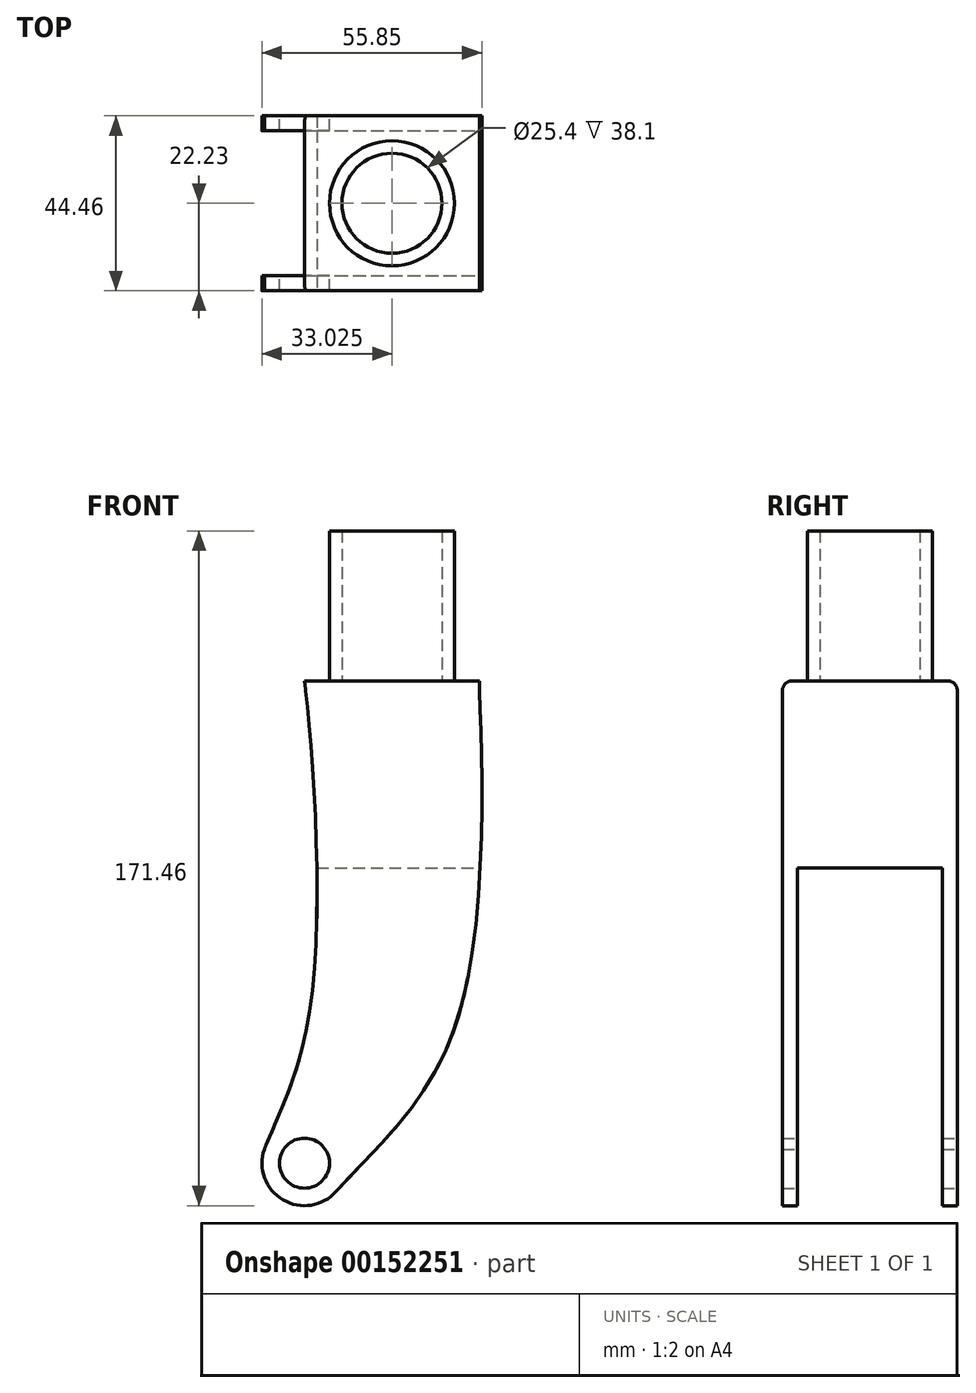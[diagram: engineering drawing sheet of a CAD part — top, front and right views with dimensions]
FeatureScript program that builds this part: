
annotation { "Feature Type Name" : "Feature", "Feature Type Description" : "" }
export const myFeature = defineFeature(function(context is Context, id is Id, definition is map)
    precondition{}
    {
        {
            var Q0;
            Q0=qCreatedBy(makeId("Front.planeOp"),FACE);
            var sketch = newSketch(context, id + "F0", { "sketchPlane" : qUnion([Q0])});
            skCircle(sketch, "E0", {"center": v(0, 0) * mm, "radius": 6.35 * mm});
            skCircle(sketch, "E1", {"center": v(0, 0) * mm, "radius": 10.8 * mm});
            skLineSegment(sketch, "E2", {"start": v(-12.15, 73.03) * mm, "end": v(17.71, 73.03) * mm, "construction": true});
            skLineSegment(sketch, "E3", {"start": v(0, 122.56) * mm, "end": v(44.45, 122.56) * mm});
            skFitSpline(sketch, "E4", {"points": [v(-10.2, 3.55) * mm, v(1.72, 41.33) * mm, v(0, 122.56) * mm], "startDerivative": vector(30.4, 74.22) * mm, "endDerivative": vector(-10.16, 76.8) * mm});
            skFitSpline(sketch, "E5", {"points": [v(8.07, -7.17) * mm, v(38.6, 35.7) * mm, v(44.45, 122.56) * mm], "startDerivative": vector(70.39, 79.18) * mm, "endDerivative": vector(-1.93, 89.44) * mm});
            skPoint(sketch, "E6", {"position": v(0, -10.8) * mm});
            skCircle(sketch, "E7", {"center": v(0, 0) * mm, "radius": 73.03 * mm, "construction": true});
            skSolve(sketch);
        }
        {
            var Q0;
            {var subQ4=sQuery(id+"F0.wireOp",EDGE,"E3");Q0=makeQuery(id+"F0.imprint","IMPRINT",FACE,{"disambiguationData":[TD([[makeQuery(id+"F0.imprint","IMPRINT",EDGE,{"derivedFrom":subQ4}),-1.0]])]});}
            var Q1;
            Q1=makeQuery(id+"F0.imprint","IMPRINT",FACE,{"disambiguationData":[TD([[makeQuery(id+"F0.imprint","IMPRINT",EDGE,{"derivedFrom":sQuery(id+"F0.wireOp",EDGE,"E0")}),-1.0]])]});
            extrude(context, id + "F1", {"entities" : qUnion([Q0, Q1]), "endBound" : BoundingType.SYMMETRIC, "depth" : 44.45 * mm});
        }
        {
            var Q0;
            Q0=makeQuery(id+"F1.opExtrude","CAP_FACE",FACE,{"disambiguationData":[OSD([sQuery(id+"F0.wireOp",EDGE,"E0"),sQuery(id+"F0.wireOp",EDGE,"E1"),sQuery(id+"F0.wireOp",EDGE,"E3"),sQuery(id+"F0.wireOp",EDGE,"E4"),sQuery(id+"F0.wireOp",EDGE,"E5")])],"isStart":false});
            var sketch = newSketch(context, id + "F2", { "sketchPlane" : qUnion([Q0])});
            skLineSegment(sketch, "E8", {"start": v(3.11, 77.02) * mm, "end": v(44.72, 77.02) * mm});
            skCircle(sketch, "E9", {"center": v(0, 0) * mm, "radius": 6.35 * mm});
            skLineSegment(sketch, "E10", {"start": v(3.15, 74.96) * mm, "end": v(44.62, 74.96) * mm});
            skLineSegment(sketch, "E11", {"start": v(44.62, 74.96) * mm, "end": v(44.72, 77.02) * mm});
            skLineSegment(sketch, "E12", {"start": v(3.11, 77.02) * mm, "end": v(3.15, 74.96) * mm});
            skSolve(sketch);
        }
        {
            var Q0;
            Q0=makeQuery(id+"F2.imprint","IMPRINT",FACE,{"disambiguationData":[TD([[makeQuery(id+"F2.imprint","IMPRINT",EDGE,{"derivedFrom":sQuery(id+"F2.wireOp",EDGE,"E9")}),-1.0]])]});
            extrude(context, id + "F3", {"entities" : qUnion([Q0]), "operationType" : NewBodyOperationType.REMOVE, "oppositeDirection" : true, "depth" : 40.64 * mm, "hasSecondDirection" : true, "secondDirectionOppositeDirection" : true, "secondDirectionDepth" : 3.8 * mm});
        }
        {
            var Q0;
            Q0=makeQuery(id+"F1.opExtrude","CAP_EDGE",EDGE,{"disambiguationData":[OSD([sQuery(id+"F0.wireOp",EDGE,"E3")])],"isStart":false});
            var Q1;
            Q1=makeQuery(id+"F1.opExtrude","CAP_EDGE",EDGE,{"disambiguationData":[OSD([sQuery(id+"F0.wireOp",EDGE,"E3")])],"isStart":true});
            fillet(context, id + "F4", {"entities" : qUnion([Q0, Q1]), "radius" : 2.54 * mm, "tangentPropagation" : true, "allowEdgeOverflow" : false});
        }
        {
            var Q0;
            Q0=makeQuery(id+"F1.opExtrude","SWEPT_FACE",FACE,{"disambiguationData":[OSD([sQuery(id+"F0.wireOp",EDGE,"E3")])]});
            var sketch = newSketch(context, id + "F5", { "sketchPlane" : qUnion([Q0])});
            skLineSegment(sketch, "E13.0", {"start": v(0.32, 22.23) * mm, "end": v(44.51, 22.23) * mm});
            skLineSegment(sketch, "E14.0", {"start": v(44.51, -22.23) * mm, "end": v(0.32, -22.23) * mm});
            skCircle(sketch, "E15", {"center": v(22.23, 0) * mm, "radius": 15.88 * mm});
            skPoint(sketch, "E15.centerSnap0", {"position": v(22.23, 19.69) * mm});
            skCircle(sketch, "E16", {"center": v(22.23, 0) * mm, "radius": 12.7 * mm});
            skSolve(sketch);
        }
        {
            var Q0;
            Q0=makeQuery(id+"F5.imprint","IMPRINT",FACE,{"disambiguationData":[TD([[makeQuery(id+"F5.imprint","IMPRINT",EDGE,{"derivedFrom":sQuery(id+"F5.wireOp",EDGE,"E16")}),-1.0]])]});
            extrude(context, id + "F6", {"entities" : qUnion([Q0]), "operationType" : NewBodyOperationType.ADD, "depth" : 38.1 * mm});
        }
    });
